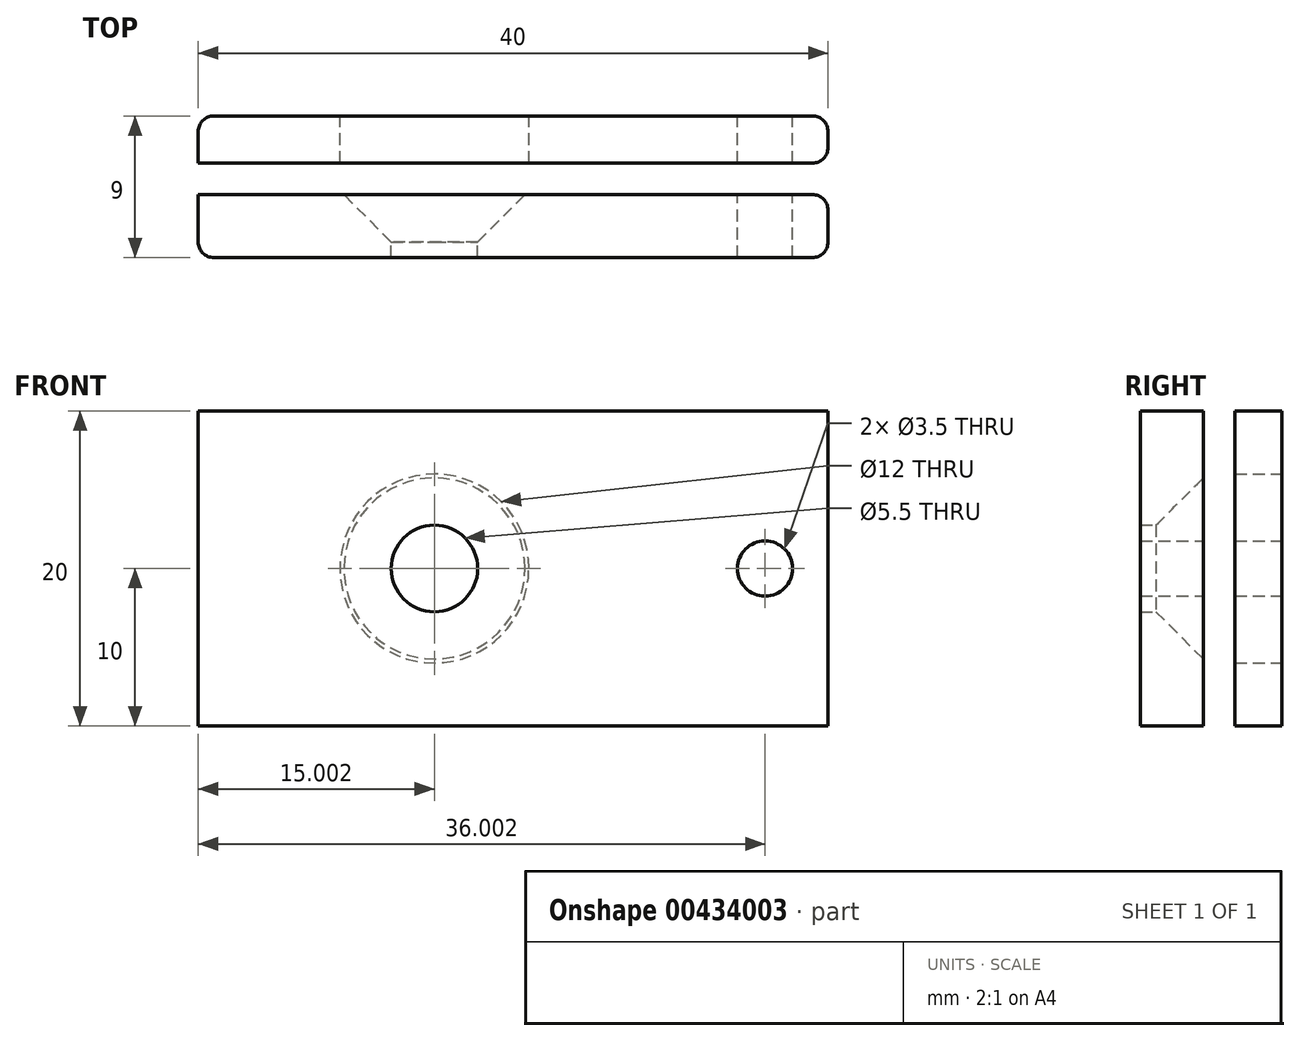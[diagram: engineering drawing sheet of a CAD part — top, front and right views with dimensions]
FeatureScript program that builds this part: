
annotation { "Feature Type Name" : "Feature", "Feature Type Description" : "" }
export const myFeature = defineFeature(function(context is Context, id is Id, definition is map)
    precondition{}
    {
        {
            var Q0;
            Q0=qCreatedBy(makeId("Top.planeOp"),FACE);
            var sketch = newSketch(context, id + "F0", { "sketchPlane" : qUnion([Q0])});
            skLineSegment(sketch, "E0.bottom", {"start": v(-12.89, 4) * mm, "end": v(27.11, 4) * mm});
            skLineSegment(sketch, "E0.top", {"start": v(-12.89, 1) * mm, "end": v(27.11, 1) * mm});
            skLineSegment(sketch, "E0.left", {"start": v(-12.89, 4) * mm, "end": v(-12.89, 1) * mm});
            skLineSegment(sketch, "E0.right", {"start": v(27.11, 4) * mm, "end": v(27.11, 1) * mm});
            skLineSegment(sketch, "E1.bottom", {"start": v(-12.89, 1) * mm, "end": v(-7.89, 1) * mm});
            skLineSegment(sketch, "E1.top", {"start": v(-12.89, -1) * mm, "end": v(-7.89, -1) * mm});
            skLineSegment(sketch, "E1.left", {"start": v(-12.89, 1) * mm, "end": v(-12.89, -1) * mm});
            skLineSegment(sketch, "E1.right", {"start": v(-7.89, 1) * mm, "end": v(-7.89, -1) * mm});
            skLineSegment(sketch, "E2.bottom", {"start": v(-12.89, -1) * mm, "end": v(27.11, -1) * mm});
            skLineSegment(sketch, "E2.top", {"start": v(-12.89, -5) * mm, "end": v(27.11, -5) * mm});
            skLineSegment(sketch, "E2.left", {"start": v(-12.89, -1) * mm, "end": v(-12.89, -5) * mm});
            skLineSegment(sketch, "E2.right", {"start": v(27.11, -1) * mm, "end": v(27.11, -5) * mm});
            skLineSegment(sketch, "E3.bottom", {"start": v(-12.89, -5) * mm, "end": v(-7.89, -5) * mm});
            skLineSegment(sketch, "E3.top", {"start": v(-12.89, -6.3) * mm, "end": v(-7.89, -6.3) * mm});
            skLineSegment(sketch, "E3.left", {"start": v(-12.89, -5) * mm, "end": v(-12.89, -6.3) * mm});
            skLineSegment(sketch, "E3.right", {"start": v(-7.89, -5) * mm, "end": v(-7.89, -6.3) * mm});
            skLineSegment(sketch, "E4.bottom", {"start": v(27.11, -5) * mm, "end": v(12.11, -5) * mm});
            skLineSegment(sketch, "E4.top", {"start": v(27.11, -6.3) * mm, "end": v(12.11, -6.3) * mm});
            skLineSegment(sketch, "E4.left", {"start": v(27.11, -5) * mm, "end": v(27.11, -6.3) * mm});
            skLineSegment(sketch, "E4.right", {"start": v(12.11, -5) * mm, "end": v(12.11, -6.3) * mm});
            skLineSegment(sketch, "E5.bottom", {"start": v(27.11, 1) * mm, "end": v(22.11, 1) * mm});
            skLineSegment(sketch, "E5.top", {"start": v(27.11, 0) * mm, "end": v(22.11, 0) * mm});
            skLineSegment(sketch, "E5.left", {"start": v(27.11, 1) * mm, "end": v(27.11, 0) * mm});
            skLineSegment(sketch, "E5.right", {"start": v(22.11, 1) * mm, "end": v(22.11, 0) * mm});
            skSolve(sketch);
        }
        {
            var Q0;
            Q0=makeQuery(id+"F0.imprint","IMPRINT",FACE,{"disambiguationData":[TD([[makeQuery(id+"F0.imprint","IMPRINT",EDGE,{"derivedFrom":sQuery(id+"F0.wireOp",EDGE,"E0.bottom")}),-1.0]])]});
            var Q1;
            Q1=makeQuery(id+"F0.imprint","IMPRINT",FACE,{"disambiguationData":[TD([[makeQuery(id+"F0.imprint","IMPRINT",EDGE,{"derivedFrom":sQuery(id+"F0.wireOp",EDGE,"E1.bottom")}),-1.0]])]});
            var Q2;
            Q2=makeQuery(id+"F0.imprint","IMPRINT",FACE,{"disambiguationData":[TD([[makeQuery(id+"F0.imprint","IMPRINT",EDGE,{"derivedFrom":sQuery(id+"F0.wireOp",EDGE,"E2.top")}),1.0]])]});
            var Q3;
            Q3=makeQuery(id+"F0.imprint","IMPRINT",FACE,{"disambiguationData":[TD([[makeQuery(id+"F0.imprint","IMPRINT",EDGE,{"derivedFrom":sQuery(id+"F0.wireOp",EDGE,"E3.bottom")}),-1.0]])]});
            var Q4;
            Q4=makeQuery(id+"F0.imprint","IMPRINT",FACE,{"disambiguationData":[TD([[makeQuery(id+"F0.imprint","IMPRINT",EDGE,{"derivedFrom":sQuery(id+"F0.wireOp",EDGE,"E4.bottom")}),1.0]])]});
            var Q5;
            Q5=makeQuery(id+"F0.imprint","IMPRINT",FACE,{"disambiguationData":[TD([[makeQuery(id+"F0.imprint","IMPRINT",EDGE,{"derivedFrom":sQuery(id+"F0.wireOp",EDGE,"E5.bottom")}),1.0]])]});
            extrude(context, id + "F1", {"entities" : qUnion([Q0, Q1, Q2, Q3, Q4, Q5]), "depth" : 20 * mm});
        }
        {
            var Q0;
            Q0=makeQuery(id+"F1.opExtrude","SWEPT_FACE",FACE,{"disambiguationData":[OSD([sQuery(id+"F0.wireOp",EDGE,"E0.bottom")])]});
            var sketch = newSketch(context, id + "F2", { "sketchPlane" : qUnion([Q0])});
            skCircle(sketch, "E6", {"center": v(-2.11, 10) * mm, "radius": 2.75 * mm});
            skPoint(sketch, "E6.centerSnap0", {"position": v(-2.11, 0) * mm});
            skPoint(sketch, "E6.centerSnap1", {"position": v(12.89, 10) * mm});
            skCircle(sketch, "E7", {"center": v(-23.11, 10) * mm, "radius": 1.75 * mm});
            skSolve(sketch);
        }
        {
            var Q0;
            Q0=makeQuery(id+"F2.imprint","IMPRINT",FACE,{"disambiguationData":[TD([[makeQuery(id+"F2.imprint","IMPRINT",EDGE,{"derivedFrom":sQuery(id+"F2.wireOp",EDGE,"E6")}),1.0]])]});
            var Q1;
            Q1=makeQuery(id+"F2.imprint","IMPRINT",FACE,{"disambiguationData":[TD([[makeQuery(id+"F2.imprint","IMPRINT",EDGE,{"derivedFrom":sQuery(id+"F2.wireOp",EDGE,"E7")}),1.0]])]});
            extrude(context, id + "F3", {"entities" : qUnion([Q0, Q1]), "operationType" : NewBodyOperationType.REMOVE, "oppositeDirection" : true, "depth" : 25 * mm});
        }
        {
            var Q0;
            Q0=makeQuery(id+"F1.opExtrude","SWEPT_EDGE",EDGE,{"disambiguationData":[OSD([sQuery(id+"F0.wireOp",EDGE,"E2.top"),sQuery(id+"F0.wireOp",EDGE,"E3.bottom"),sQuery(id+"F0.wireOp",EDGE,"E3.right")])]});
            var Q1;
            Q1=makeQuery(id+"F1.opExtrude","SWEPT_EDGE",EDGE,{"disambiguationData":[OSD([sQuery(id+"F0.wireOp",EDGE,"E2.top"),sQuery(id+"F0.wireOp",EDGE,"E4.bottom"),sQuery(id+"F0.wireOp",EDGE,"E4.right")])]});
            var Q2;
            Q2=makeQuery(id+"F1.opExtrude","SWEPT_EDGE",EDGE,{"disambiguationData":[OSD([sQuery(id+"F0.wireOp",EDGE,"E3.top"),sQuery(id+"F0.wireOp",EDGE,"E3.left")])]});
            var Q3;
            Q3=makeQuery(id+"F1.opExtrude","SWEPT_EDGE",EDGE,{"disambiguationData":[OSD([sQuery(id+"F0.wireOp",EDGE,"E4.top"),sQuery(id+"F0.wireOp",EDGE,"E4.left")])]});
            var Q4;
            Q4=makeQuery(id+"F1.opExtrude","SWEPT_EDGE",EDGE,{"disambiguationData":[OSD([sQuery(id+"F0.wireOp",EDGE,"E2.bottom"),sQuery(id+"F0.wireOp",EDGE,"E2.right")])]});
            var Q5;
            Q5=makeQuery(id+"F1.opExtrude","SWEPT_EDGE",EDGE,{"disambiguationData":[OSD([sQuery(id+"F0.wireOp",EDGE,"E0.top"),sQuery(id+"F0.wireOp",EDGE,"E0.right")])]});
            var Q6;
            Q6=makeQuery(id+"F1.opExtrude","SWEPT_EDGE",EDGE,{"disambiguationData":[OSD([sQuery(id+"F0.wireOp",EDGE,"E0.bottom"),sQuery(id+"F0.wireOp",EDGE,"E0.right")])]});
            var Q7;
            Q7=makeQuery(id+"F1.opExtrude","SWEPT_EDGE",EDGE,{"disambiguationData":[OSD([sQuery(id+"F0.wireOp",EDGE,"E0.bottom"),sQuery(id+"F0.wireOp",EDGE,"E0.left")])]});
            var Q8;
            Q8=makeQuery(id+"F1.opExtrude","SWEPT_EDGE",EDGE,{"disambiguationData":[OSD([sQuery(id+"F0.wireOp",EDGE,"E5.top"),sQuery(id+"F0.wireOp",EDGE,"E5.left")])]});
            var Q9;
            {var subQ0=sQuery(id+"F0.wireOp",EDGE,"E5.right");var subQ1=sQuery(id+"F0.wireOp",EDGE,"E5.top");Q9=makeQuery(id+"F3.boolean.opBoolean","SPLIT",EDGE,{"disambiguationData":[TD([makeQuery(id+"F1.opExtrude","CAP_FACE",FACE,{"disambiguationData":[OSD([sQuery(id+"F0.wireOp",EDGE,"E0.bottom"),sQuery(id+"F0.wireOp",EDGE,"E0.top"),sQuery(id+"F0.wireOp",EDGE,"E0.left"),sQuery(id+"F0.wireOp",EDGE,"E0.right"),sQuery(id+"F0.wireOp",EDGE,"E1.left"),sQuery(id+"F0.wireOp",EDGE,"E1.right"),sQuery(id+"F0.wireOp",EDGE,"E2.bottom"),sQuery(id+"F0.wireOp",EDGE,"E2.top"),sQuery(id+"F0.wireOp",EDGE,"E2.left"),sQuery(id+"F0.wireOp",EDGE,"E2.right"),sQuery(id+"F0.wireOp",EDGE,"E3.top"),sQuery(id+"F0.wireOp",EDGE,"E3.left"),sQuery(id+"F0.wireOp",EDGE,"E3.right"),sQuery(id+"F0.wireOp",EDGE,"E4.top"),sQuery(id+"F0.wireOp",EDGE,"E4.left"),sQuery(id+"F0.wireOp",EDGE,"E4.right"),subQ1,sQuery(id+"F0.wireOp",EDGE,"E5.left"),subQ0])],"isStart":false})])],"derivedFrom":makeQuery(id+"F1.opExtrude","SWEPT_EDGE",EDGE,{"disambiguationData":[OSD([subQ1,subQ0])]})});}
            var Q10;
            {var subQ0=sQuery(id+"F0.wireOp",EDGE,"E5.right");var subQ1=sQuery(id+"F0.wireOp",EDGE,"E5.top");Q10=makeQuery(id+"F3.boolean.opBoolean","SPLIT",EDGE,{"disambiguationData":[TD([makeQuery(id+"F1.opExtrude","CAP_FACE",FACE,{"disambiguationData":[OSD([sQuery(id+"F0.wireOp",EDGE,"E0.bottom"),sQuery(id+"F0.wireOp",EDGE,"E0.top"),sQuery(id+"F0.wireOp",EDGE,"E0.left"),sQuery(id+"F0.wireOp",EDGE,"E0.right"),sQuery(id+"F0.wireOp",EDGE,"E1.left"),sQuery(id+"F0.wireOp",EDGE,"E1.right"),sQuery(id+"F0.wireOp",EDGE,"E2.bottom"),sQuery(id+"F0.wireOp",EDGE,"E2.top"),sQuery(id+"F0.wireOp",EDGE,"E2.left"),sQuery(id+"F0.wireOp",EDGE,"E2.right"),sQuery(id+"F0.wireOp",EDGE,"E3.top"),sQuery(id+"F0.wireOp",EDGE,"E3.left"),sQuery(id+"F0.wireOp",EDGE,"E3.right"),sQuery(id+"F0.wireOp",EDGE,"E4.top"),sQuery(id+"F0.wireOp",EDGE,"E4.left"),sQuery(id+"F0.wireOp",EDGE,"E4.right"),subQ1,sQuery(id+"F0.wireOp",EDGE,"E5.left"),subQ0])],"isStart":true})])],"derivedFrom":makeQuery(id+"F1.opExtrude","SWEPT_EDGE",EDGE,{"disambiguationData":[OSD([subQ1,subQ0])]})});}
            fillet(context, id + "F4", {"entities" : qUnion([Q0, Q1, Q2, Q3, Q4, Q5, Q6, Q7, Q8, Q9, Q10]), "radius" : 1 * mm, "tangentPropagation" : true, "allowEdgeOverflow" : false});
        }
        {
            var Q0;
            Q0=makeQuery(id+"F1.opExtrude","SWEPT_FACE",FACE,{"disambiguationData":[OSD([sQuery(id+"F0.wireOp",EDGE,"E0.bottom")])]});
            var sketch = newSketch(context, id + "F5", { "sketchPlane" : qUnion([Q0])});
            skCircle(sketch, "E8", {"center": v(-2.11, 10) * mm, "radius": 6 * mm});
            skSolve(sketch);
        }
        {
            var Q0;
            Q0=makeQuery(id+"F5.imprint","IMPRINT",FACE,{"disambiguationData":[TD([[makeQuery(id+"F5.imprint","IMPRINT",EDGE,{"derivedFrom":sQuery(id+"F5.wireOp",EDGE,"E8")}),1.0]])]});
            extrude(context, id + "F6", {"entities" : qUnion([Q0]), "operationType" : NewBodyOperationType.REMOVE, "oppositeDirection" : true, "depth" : 5 * mm});
        }
        {
            var Q0;
            Q0=makeQuery(id+"F3.boolean.opBoolean","INTERSECT",EDGE,{"derivedFrom":[makeQuery(id+"F1.opExtrude","SWEPT_FACE",FACE,{"disambiguationData":[OSD([sQuery(id+"F0.wireOp",EDGE,"E2.bottom")])]}),makeQuery(id+"F3.opExtrude","SWEPT_FACE",FACE,{"disambiguationData":[OSD([sQuery(id+"F2.wireOp",EDGE,"E6")])]})]});
            chamfer(context, id + "F7", {"entities" : qUnion([Q0]), "width" : 3 * mm, "tangentPropagation" : true});
        }
    });
